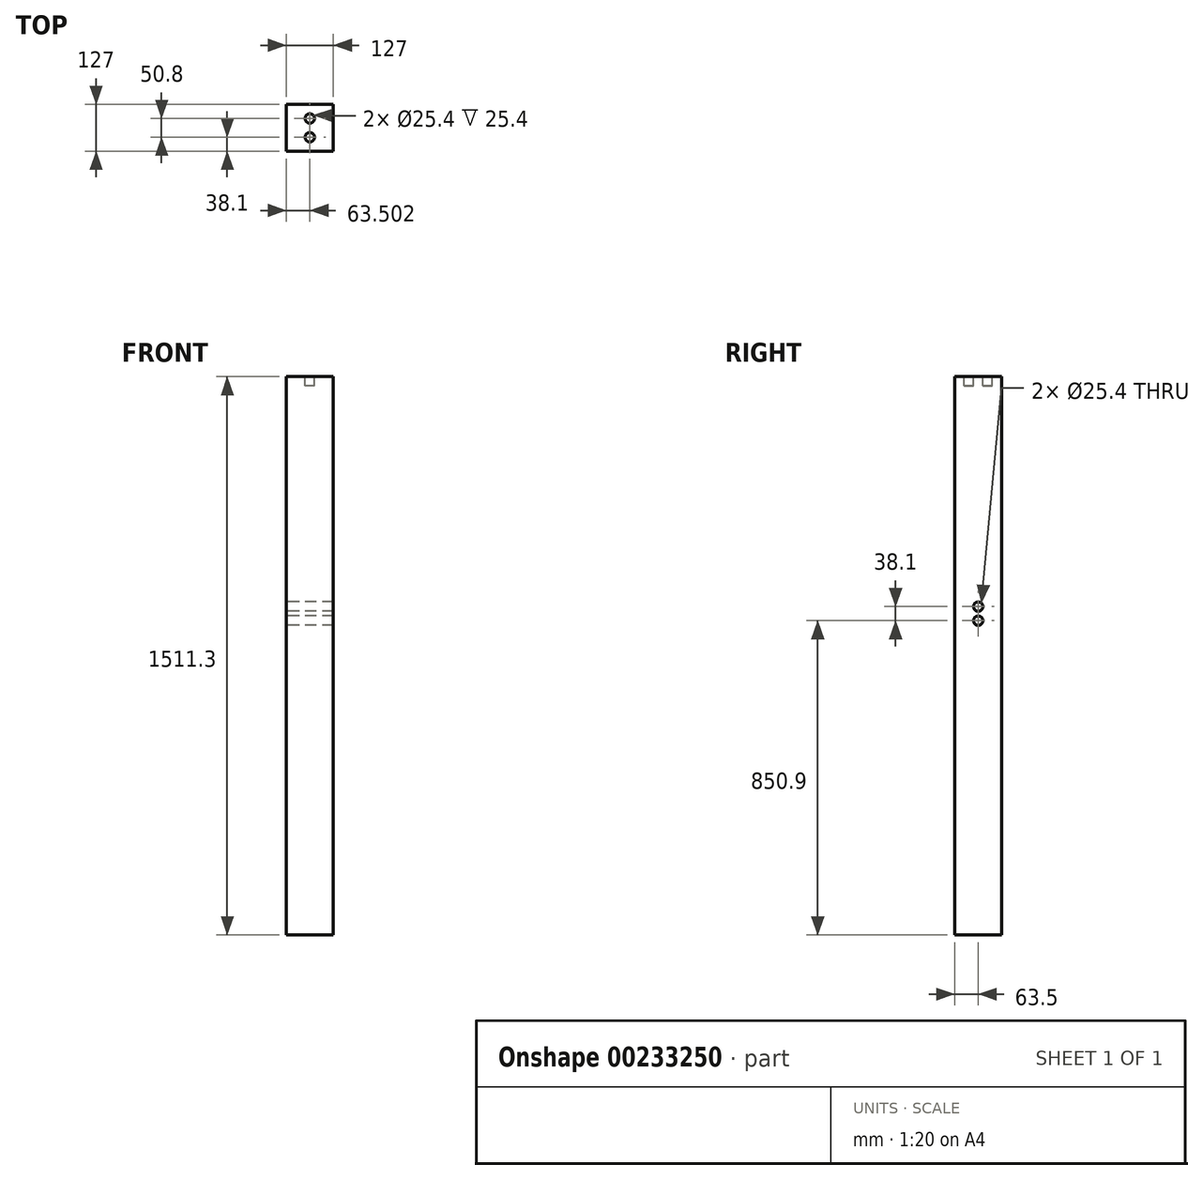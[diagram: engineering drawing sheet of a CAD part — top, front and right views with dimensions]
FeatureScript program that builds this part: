
annotation { "Feature Type Name" : "Feature", "Feature Type Description" : "" }
export const myFeature = defineFeature(function(context is Context, id is Id, definition is map)
    precondition{}
    {
        {
            var Q0;
            Q0=qCreatedBy(makeId("Front.planeOp"),FACE);
            var sketch = newSketch(context, id + "F0", { "sketchPlane" : qUnion([Q0])});
            skLineSegment(sketch, "E0.bottom", {"start": v(-91, 1430.97) * mm, "end": v(36, 1430.97) * mm});
            skLineSegment(sketch, "E0.top", {"start": v(-91, -80.33) * mm, "end": v(36, -80.33) * mm});
            skLineSegment(sketch, "E0.left", {"start": v(-91, 1430.97) * mm, "end": v(-91, -80.33) * mm});
            skLineSegment(sketch, "E0.right", {"start": v(36, 1430.97) * mm, "end": v(36, -80.33) * mm});
            skSolve(sketch);
        }
        {
            var Q0;
            Q0 = qSketchRegion(id + "F0", true);
            extrude(context, id + "F1", {"entities" : qUnion([Q0]), "depth" : 127 * mm});
        }
        {
            var Q0;
            Q0=makeQuery(id+"F1.opExtrude","SWEPT_FACE",FACE,{"disambiguationData":[OSD([sQuery(id+"F0.wireOp",EDGE,"E0.bottom")])]});
            var sketch = newSketch(context, id + "F2", { "sketchPlane" : qUnion([Q0])});
            skCircle(sketch, "E1", {"center": v(-27.5, -38.1) * mm, "radius": 12.7 * mm});
            skCircle(sketch, "E2", {"center": v(-27.5, -88.9) * mm, "radius": 12.7 * mm});
            skSolve(sketch);
        }
        {
            var Q0;
            Q0 = qSketchRegion(id + "F2", true);
            extrude(context, id + "F3", {"entities" : qUnion([Q0]), "operationType" : NewBodyOperationType.REMOVE, "oppositeDirection" : true, "depth" : 25.4 * mm});
        }
        {
            var Q0;
            Q0=makeQuery(id+"F1.opExtrude","SWEPT_FACE",FACE,{"disambiguationData":[OSD([sQuery(id+"F0.wireOp",EDGE,"E0.left")])]});
            var sketch = newSketch(context, id + "F4", { "sketchPlane" : qUnion([Q0])});
            skCircle(sketch, "E3", {"center": v(63.5, 770.57) * mm, "radius": 12.7 * mm});
            skCircle(sketch, "E4", {"center": v(63.5, 808.67) * mm, "radius": 12.7 * mm});
            skSolve(sketch);
        }
        {
            var Q0;
            Q0 = qSketchRegion(id + "F4", true);
            extrude(context, id + "F5", {"entities" : qUnion([Q0]), "operationType" : NewBodyOperationType.REMOVE, "oppositeDirection" : true, "depth" : 127 * mm});
        }
    });
